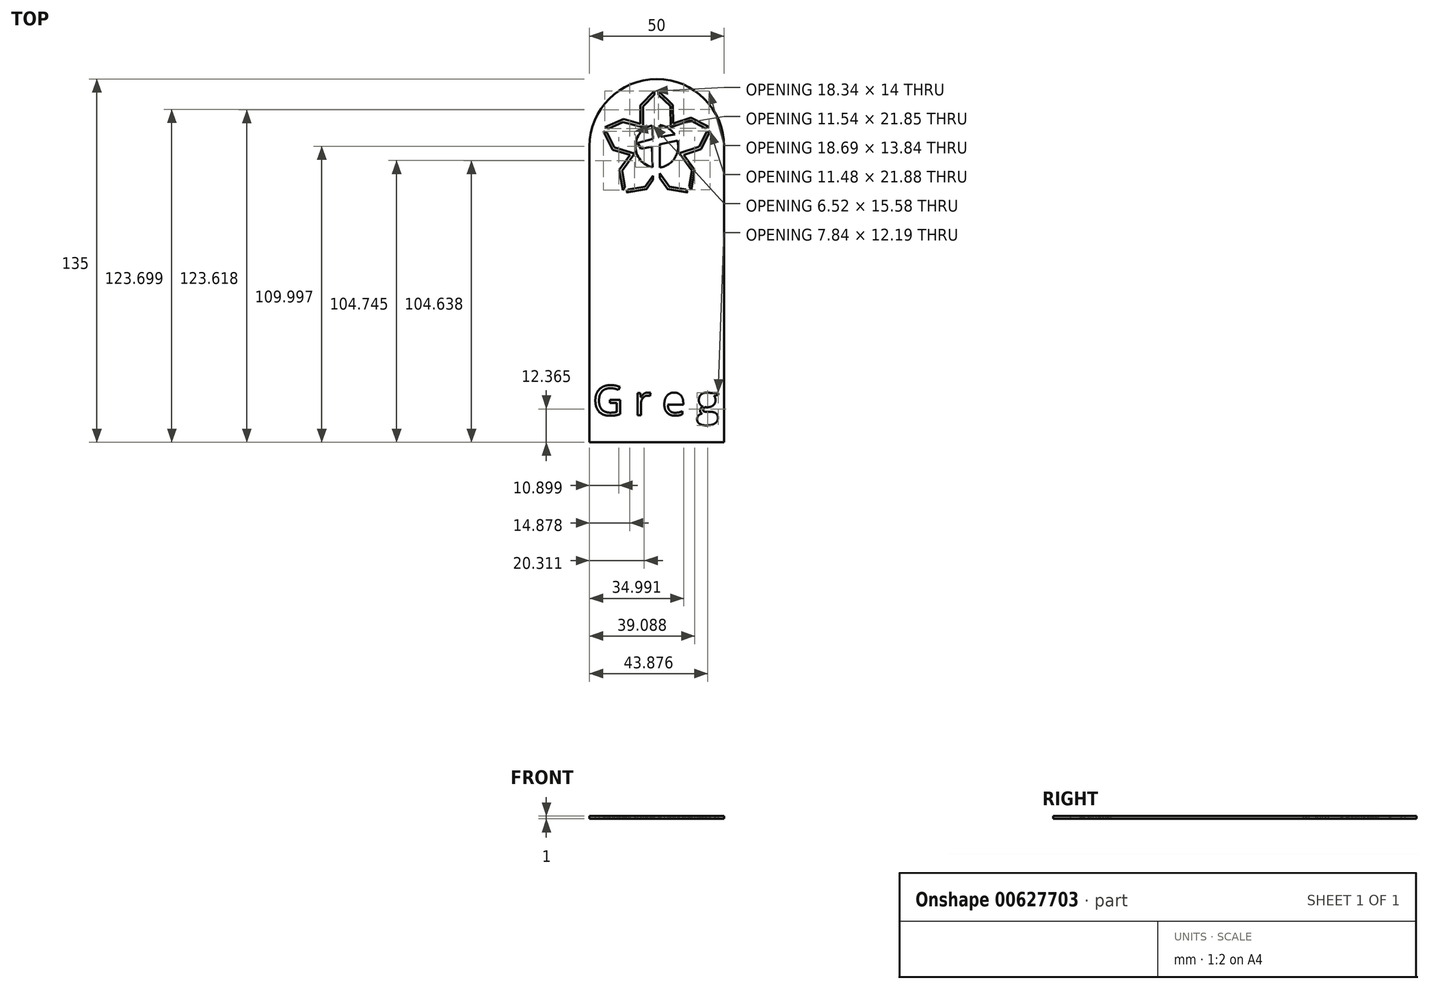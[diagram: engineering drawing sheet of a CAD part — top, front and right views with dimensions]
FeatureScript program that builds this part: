
annotation { "Feature Type Name" : "Feature", "Feature Type Description" : "" }
export const myFeature = defineFeature(function(context is Context, id is Id, definition is map)
    precondition{}
    {
        {
            var Q0;
            Q0=qCreatedBy(makeId("Top.planeOp"),FACE);
            var sketch = newSketch(context, id + "F0", { "sketchPlane" : qUnion([Q0])});
            skArc(sketch, "E0", {"start": v(1.43, 12.5) * mm, "mid": v(-23.57, 37.5) * mm, "end": v(-48.57, 12.5) * mm});
            skLineSegment(sketch, "E1", {"start": v(-28.74, 19.57) * mm, "end": v(-28.74, 27.36) * mm});
            skLineSegment(sketch, "E2", {"start": v(-28.74, 27.36) * mm, "end": v(-24.52, 31.68) * mm});
            skLineSegment(sketch, "E3", {"start": v(-22.92, 31.71) * mm, "end": v(-18.59, 27.41) * mm});
            skLineSegment(sketch, "E4", {"start": v(-18.59, 27.41) * mm, "end": v(-18.45, 19.6) * mm});
            skLineSegment(sketch, "E5", {"start": v(-18.45, 19.6) * mm, "end": v(-11.04, 22.13) * mm});
            skLineSegment(sketch, "E6", {"start": v(-11.04, 22.13) * mm, "end": v(-5.57, 19.28) * mm});
            skLineSegment(sketch, "E7", {"start": v(-5.08, 17.75) * mm, "end": v(-7.83, 12.32) * mm});
            skLineSegment(sketch, "E8", {"start": v(-7.83, 12.32) * mm, "end": v(-15.22, 9.9) * mm});
            skLineSegment(sketch, "E9", {"start": v(-15.22, 9.9) * mm, "end": v(-10.56, 3.45) * mm});
            skLineSegment(sketch, "E10", {"start": v(-10.56, 3.45) * mm, "end": v(-11.6, -2.55) * mm});
            skLineSegment(sketch, "E11", {"start": v(-12.9, -3.48) * mm, "end": v(-18.94, -2.5) * mm});
            skLineSegment(sketch, "E12", {"start": v(-18.94, -2.5) * mm, "end": v(-22.48, 2.4) * mm});
            skLineSegment(sketch, "E13", {"start": v(-27.97, -2.5) * mm, "end": v(-34.11, -3.56) * mm});
            skLineSegment(sketch, "E14", {"start": v(-35.42, -2.63) * mm, "end": v(-36.47, 3.45) * mm});
            skLineSegment(sketch, "E15", {"start": v(-36.47, 3.45) * mm, "end": v(-31.9, 9.82) * mm});
            skLineSegment(sketch, "E16", {"start": v(-31.9, 9.82) * mm, "end": v(-39.32, 12.08) * mm});
            skLineSegment(sketch, "E17", {"start": v(-39.32, 12.08) * mm, "end": v(-42.1, 17.63) * mm});
            skLineSegment(sketch, "E18", {"start": v(-41.52, 19.12) * mm, "end": v(-36.16, 21.53) * mm});
            skLineSegment(sketch, "E19", {"start": v(-36.16, 21.53) * mm, "end": v(-28.74, 19.57) * mm});
            skLineSegment(sketch, "E20", {"start": v(-22.45, 20.38) * mm, "end": v(-22.07, 16.04) * mm});
            skLineSegment(sketch, "E21", {"start": v(-22.07, 16.04) * mm, "end": v(-16.93, 16.87) * mm});
            skLineSegment(sketch, "E22", {"start": v(-15.91, 14.64) * mm, "end": v(-22.48, 13.25) * mm});
            skLineSegment(sketch, "E23", {"start": v(-22.48, 13.25) * mm, "end": v(-22.48, 4.63) * mm});
            skLineSegment(sketch, "E24", {"start": v(-24.95, -0.02) * mm, "end": v(-24.96, 0) * mm});
            skLineSegment(sketch, "E25", {"start": v(-24.96, 0) * mm, "end": v(-25.01, 1.6) * mm});
            skLineSegment(sketch, "E26", {"start": v(-25.4, 12.38) * mm, "end": v(-29.46, 11.63) * mm});
            skLineSegment(sketch, "E27", {"start": v(-29.46, 11.63) * mm, "end": v(-30.7, 13.78) * mm});
            skLineSegment(sketch, "E28", {"start": v(-30.7, 13.78) * mm, "end": v(-25, 15.25) * mm});
            skLineSegment(sketch, "E29", {"start": v(-25, 15.25) * mm, "end": v(-25.2, 20.29) * mm});
            skLineSegment(sketch, "E30", {"start": v(-48.57, 12.5) * mm, "end": v(-48.57, -97.5) * mm});
            skLineSegment(sketch, "E31", {"start": v(1.43, 12.5) * mm, "end": v(1.43, -97.5) * mm});
            skLineSegment(sketch, "E32", {"start": v(-48.57, -97.5) * mm, "end": v(1.43, -97.5) * mm});
            skLineSegment(sketch, "E33", {"start": v(-34.93, -4.7) * mm, "end": v(-27.4, -3.42) * mm});
            skLineSegment(sketch, "E34", {"start": v(-37.52, 3.69) * mm, "end": v(-36.24, -3.79) * mm});
            skLineSegment(sketch, "E35", {"start": v(-33.52, 9.27) * mm, "end": v(-37.52, 3.69) * mm});
            skLineSegment(sketch, "E36", {"start": v(-27.4, -3.42) * mm, "end": v(-24.95, -0.02) * mm});
            skLineSegment(sketch, "E37", {"start": v(-40.03, 11.25) * mm, "end": v(-33.52, 9.27) * mm});
            skLineSegment(sketch, "E38", {"start": v(-43.44, 18.06) * mm, "end": v(-40.03, 11.25) * mm});
            skLineSegment(sketch, "E39", {"start": v(-42.86, 19.56) * mm, "end": v(-35.93, 22.66) * mm});
            skLineSegment(sketch, "E40", {"start": v(-29.74, 27.76) * mm, "end": v(-29.74, 20.84) * mm});
            skLineSegment(sketch, "E41", {"start": v(-29.74, 27.76) * mm, "end": v(-24.52, 33.12) * mm});
            skLineSegment(sketch, "E42", {"start": v(-22.92, 33.12) * mm, "end": v(-17.6, 27.84) * mm});
            skLineSegment(sketch, "E43", {"start": v(-17.6, 27.84) * mm, "end": v(-17.48, 21) * mm});
            skLineSegment(sketch, "E44", {"start": v(-10.96, 23.21) * mm, "end": v(-4.23, 19.7) * mm});
            skLineSegment(sketch, "E45", {"start": v(-3.74, 18.18) * mm, "end": v(-7.12, 11.5) * mm});
            skLineSegment(sketch, "E46", {"start": v(-13.6, 9.37) * mm, "end": v(-9.5, 3.7) * mm});
            skLineSegment(sketch, "E47", {"start": v(-9.5, 3.7) * mm, "end": v(-10.78, -3.7) * mm});
            skLineSegment(sketch, "E48", {"start": v(-19.51, -3.42) * mm, "end": v(-12.09, -4.62) * mm});
            skLineSegment(sketch, "E49.trimOffspring", {"start": v(-19.51, -3.42) * mm, "end": v(-22.48, 0.7) * mm});
            skLineSegment(sketch, "E50.trimOffspring", {"start": v(-13.6, 9.37) * mm, "end": v(-7.12, 11.5) * mm});
            skLineSegment(sketch, "E51.trimOffspring", {"start": v(-35.93, 22.66) * mm, "end": v(-29.74, 20.84) * mm});
            skLineSegment(sketch, "E52.trimOffspring", {"start": v(-17.48, 21) * mm, "end": v(-10.96, 23.21) * mm});
            skLineSegment(sketch, "E53.trimOffspring", {"start": v(-25.01, 1.6) * mm, "end": v(-27.97, -2.5) * mm});
            skLineSegment(sketch, "E54.trimOffspring", {"start": v(-25.12, 4.7) * mm, "end": v(-25.4, 12.38) * mm});
            skLineSegment(sketch, "E55.trimOffspring", {"start": v(-22.48, 2.4) * mm, "end": v(-22.48, 0.7) * mm});
            skText(sketch, "E56", { "text": "G r e g", "fontName": "OpenSans-Regular.ttf"});
            skLineSegment(sketch, "E57", {"start": v(-36.24, -3.79) * mm, "end": v(-35.42, -2.63) * mm});
            skLineSegment(sketch, "E58", {"start": v(-34.93, -4.7) * mm, "end": v(-34.11, -3.56) * mm});
            skLineSegment(sketch, "E59", {"start": v(-12.9, -3.48) * mm, "end": v(-12.09, -4.62) * mm});
            skLineSegment(sketch, "E60", {"start": v(-11.6, -2.55) * mm, "end": v(-10.78, -3.7) * mm});
            skArc(sketch, "E61", {"start": v(-25.2, 20.29) * mm, "mid": v(-31.52, 12.47) * mm, "end": v(-25.12, 4.7) * mm});
            skArc(sketch, "E62.trimOffspring", {"start": v(-16.93, 16.87) * mm, "mid": v(-19.31, 19.22) * mm, "end": v(-22.45, 20.38) * mm});
            skArc(sketch, "E63.trimOffspring", {"start": v(-22.48, 4.63) * mm, "mid": v(-16.93, 8.14) * mm, "end": v(-15.91, 14.64) * mm});
            skLineSegment(sketch, "E64", {"start": v(-5.08, 17.75) * mm, "end": v(-3.74, 18.18) * mm});
            skLineSegment(sketch, "E65", {"start": v(-5.57, 19.28) * mm, "end": v(-4.23, 19.7) * mm});
            skLineSegment(sketch, "E66", {"start": v(-22.92, 33.12) * mm, "end": v(-22.92, 31.71) * mm});
            skLineSegment(sketch, "E67", {"start": v(-24.52, 33.12) * mm, "end": v(-24.52, 31.68) * mm});
            skLineSegment(sketch, "E68", {"start": v(-42.86, 19.56) * mm, "end": v(-41.52, 19.12) * mm});
            skLineSegment(sketch, "E69", {"start": v(-43.44, 18.06) * mm, "end": v(-42.1, 17.63) * mm});
            const initialGuessF0  = {"E56": [-0.04737, -0.0875, 1, 0, 0.01118]};
            skSetInitialGuess(sketch, initialGuessF0);
            skSolve(sketch);
        }
        {
            var Q0;
            Q0=makeQuery(id+"F0.imprint","IMPRINT",FACE,{"disambiguationData":[TD([[makeQuery(id+"F0.imprint","IMPRINT",EDGE,{"derivedFrom":sQuery(id+"F0.wireOp",EDGE,"E0")}),1.0]])]});
            extrude(context, id + "F1", {"entities" : qUnion([Q0]), "depth" : 1 * mm, "offsetDistance" : 25 * mm});
        }
    });
